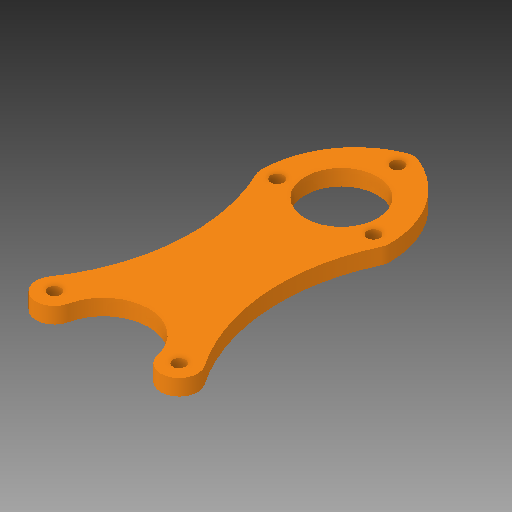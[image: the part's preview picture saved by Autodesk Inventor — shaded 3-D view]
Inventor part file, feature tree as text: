
AUTODESK INVENTOR PART (.ipt)
format: ipt  version: 2017 SP1 (Build 210196100, 196)  size: 151,552 bytes
history: native  units: in
note: dims shown in document units (in); Inventor stores cm internally (conversion verified against a paired STEP export)
features: extrude x1, sketch x1
ambient origin geometry x8: Origin, YZ Plane, XZ Plane, XY Plane, X Axis, Y Axis, Z Axis, Center Point
bodies: Solid1 (feature_tree)
feature tree (2):
  extrude  "Extrusion1"  Depth=0.25in
  sketch  "Sketch1"  dims[d0=1.125in d1=0.625in d3=0.196in d4=3.501in d5=4.0in d7=2.0in d8=0.2in d9=0.375in d10=1.5in d12=0.25in d15=0.25in d16=0.0in d18=1.125in d19=0.375in d20=60.0deg d23=1.375in d25=0.1875in d26=1.375in d27=1.0in]
